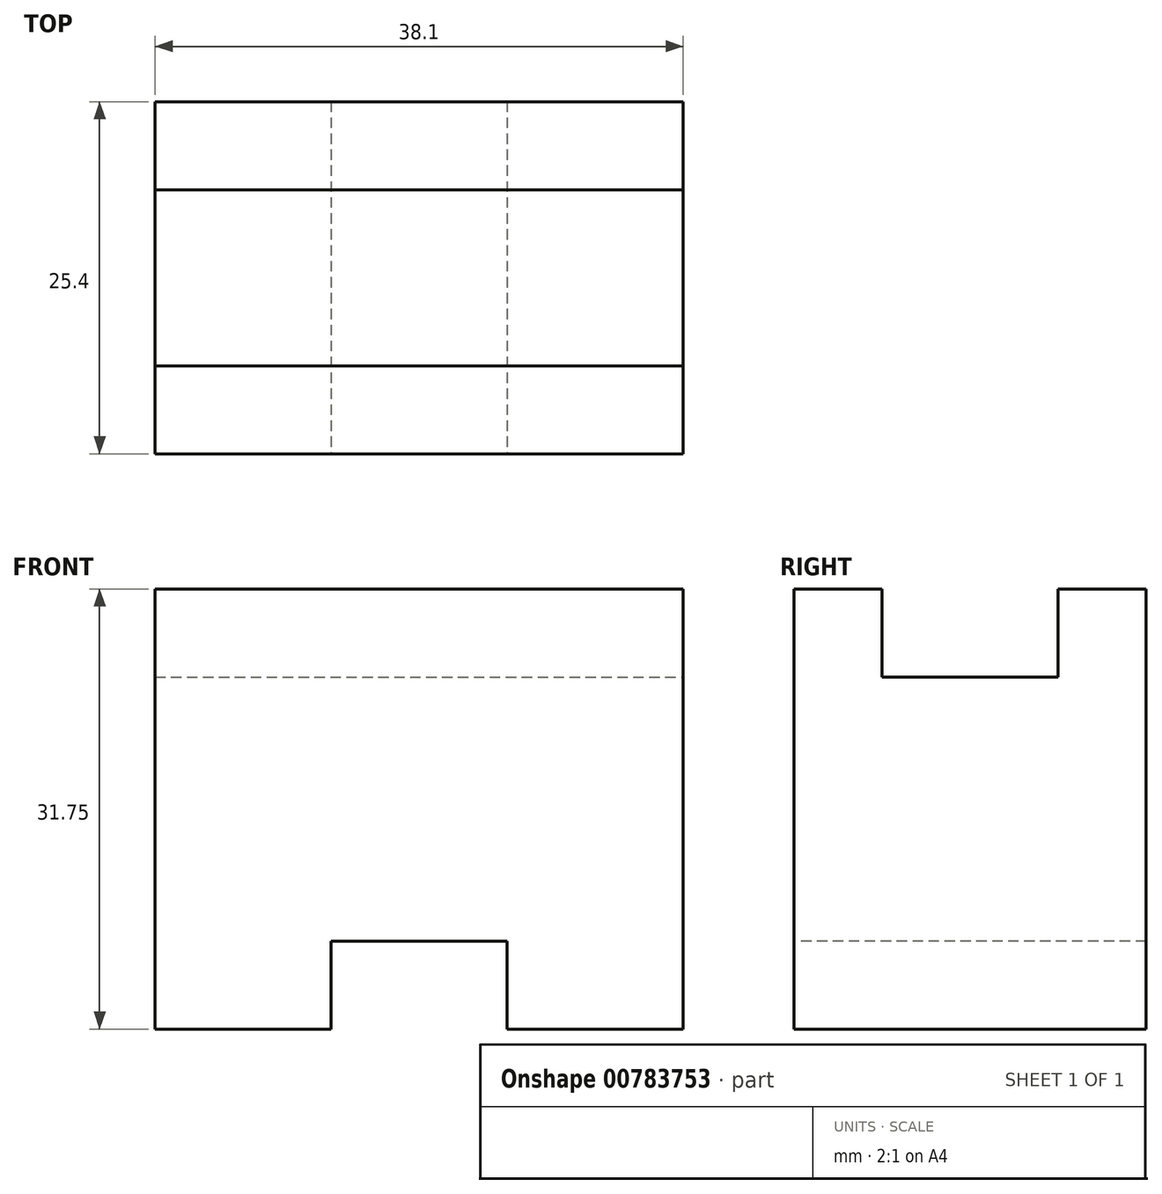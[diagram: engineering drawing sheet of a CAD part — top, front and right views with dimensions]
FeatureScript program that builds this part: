
annotation { "Feature Type Name" : "Feature", "Feature Type Description" : "" }
export const myFeature = defineFeature(function(context is Context, id is Id, definition is map)
    precondition{}
    {
        {
            var Q0;
            Q0=qCreatedBy(makeId("Front.planeOp"),FACE);
            var sketch = newSketch(context, id + "F0", { "sketchPlane" : qUnion([Q0])});
            skLineSegment(sketch, "E0", {"start": v(0, 0) * mm, "end": v(38.1, 0) * mm});
            skLineSegment(sketch, "E1", {"start": v(38.1, 0) * mm, "end": v(38.1, 31.75) * mm});
            skLineSegment(sketch, "E2", {"start": v(38.1, 31.75) * mm, "end": v(0, 31.75) * mm});
            skLineSegment(sketch, "E3", {"start": v(0, 31.75) * mm, "end": v(0, 0) * mm});
            skSolve(sketch);
        }
        {
            var Q0;
            Q0=makeQuery(id+"F0.imprint","IMPRINT",FACE,{"disambiguationData":[TD([[makeQuery(id+"F0.imprint","IMPRINT",EDGE,{"derivedFrom":sQuery(id+"F0.wireOp",EDGE,"E0")}),1.0]])]});
            extrude(context, id + "F1", {"entities" : qUnion([Q0]), "depth" : 25.4 * mm, "offsetDistance" : 25.4 * mm});
        }
        {
            var Q0;
            Q0=makeQuery(id+"F1.opExtrude","CAP_FACE",FACE,{"disambiguationData":[OSD([sQuery(id+"F0.wireOp",EDGE,"E0"),sQuery(id+"F0.wireOp",EDGE,"E1"),sQuery(id+"F0.wireOp",EDGE,"E2"),sQuery(id+"F0.wireOp",EDGE,"E3")])],"isStart":false});
            var sketch = newSketch(context, id + "F2", { "sketchPlane" : qUnion([Q0])});
            skLineSegment(sketch, "E4", {"start": v(0, 0) * mm, "end": v(12.7, 0) * mm});
            skLineSegment(sketch, "E5", {"start": v(12.7, 0) * mm, "end": v(12.7, 6.35) * mm});
            skLineSegment(sketch, "E6", {"start": v(12.7, 6.35) * mm, "end": v(25.4, 6.35) * mm});
            skLineSegment(sketch, "E7", {"start": v(25.4, 6.35) * mm, "end": v(25.4, 0) * mm});
            skLineSegment(sketch, "E8", {"start": v(25.4, 0) * mm, "end": v(38.1, 0) * mm});
            skSolve(sketch);
        }
        {
            var Q0;
            Q0 = qSketchRegion(id + "F2", true);
            var Q1;
            {var subQ0=sQuery(id+"F2.wireOp",EDGE,"E5");Q1=makeQuery(id+"F2.imprint","IMPRINT",FACE,{"disambiguationData":[TD([[makeQuery(id+"F2.imprint","IMPRINT",EDGE,{"derivedFrom":subQ0}),-1.0]])]});}
            extrude(context, id + "F3", {"entities" : qUnion([Q0, Q1]), "operationType" : NewBodyOperationType.REMOVE, "oppositeDirection" : true, "depth" : 25.4 * mm, "offsetDistance" : 25.4 * mm});
        }
        {
            var Q0;
            Q0=makeQuery(id+"F1.opExtrude","SWEPT_FACE",FACE,{"disambiguationData":[OSD([sQuery(id+"F0.wireOp",EDGE,"E1")])]});
            var sketch = newSketch(context, id + "F4", { "sketchPlane" : qUnion([Q0])});
            skLineSegment(sketch, "E9", {"start": v(-25.4, 31.75) * mm, "end": v(-19.05, 31.75) * mm});
            skLineSegment(sketch, "E10", {"start": v(-19.05, 31.75) * mm, "end": v(-19.05, 25.4) * mm});
            skLineSegment(sketch, "E11", {"start": v(-19.05, 25.4) * mm, "end": v(-6.35, 25.4) * mm});
            skLineSegment(sketch, "E12", {"start": v(-6.35, 25.4) * mm, "end": v(-6.35, 31.75) * mm});
            skLineSegment(sketch, "E13", {"start": v(-6.35, 31.75) * mm, "end": v(0, 31.75) * mm});
            skSolve(sketch);
        }
        {
            var Q0;
            Q0 = qSketchRegion(id + "F4", true);
            var Q1;
            {var subQ0=sQuery(id+"F4.wireOp",EDGE,"E10");Q1=makeQuery(id+"F4.imprint","IMPRINT",FACE,{"disambiguationData":[TD([[makeQuery(id+"F4.imprint","IMPRINT",EDGE,{"derivedFrom":subQ0}),1.0]])]});}
            extrude(context, id + "F5", {"entities" : qUnion([Q0, Q1]), "operationType" : NewBodyOperationType.REMOVE, "oppositeDirection" : true, "depth" : 38.1 * mm, "offsetDistance" : 25.4 * mm});
        }
    });
